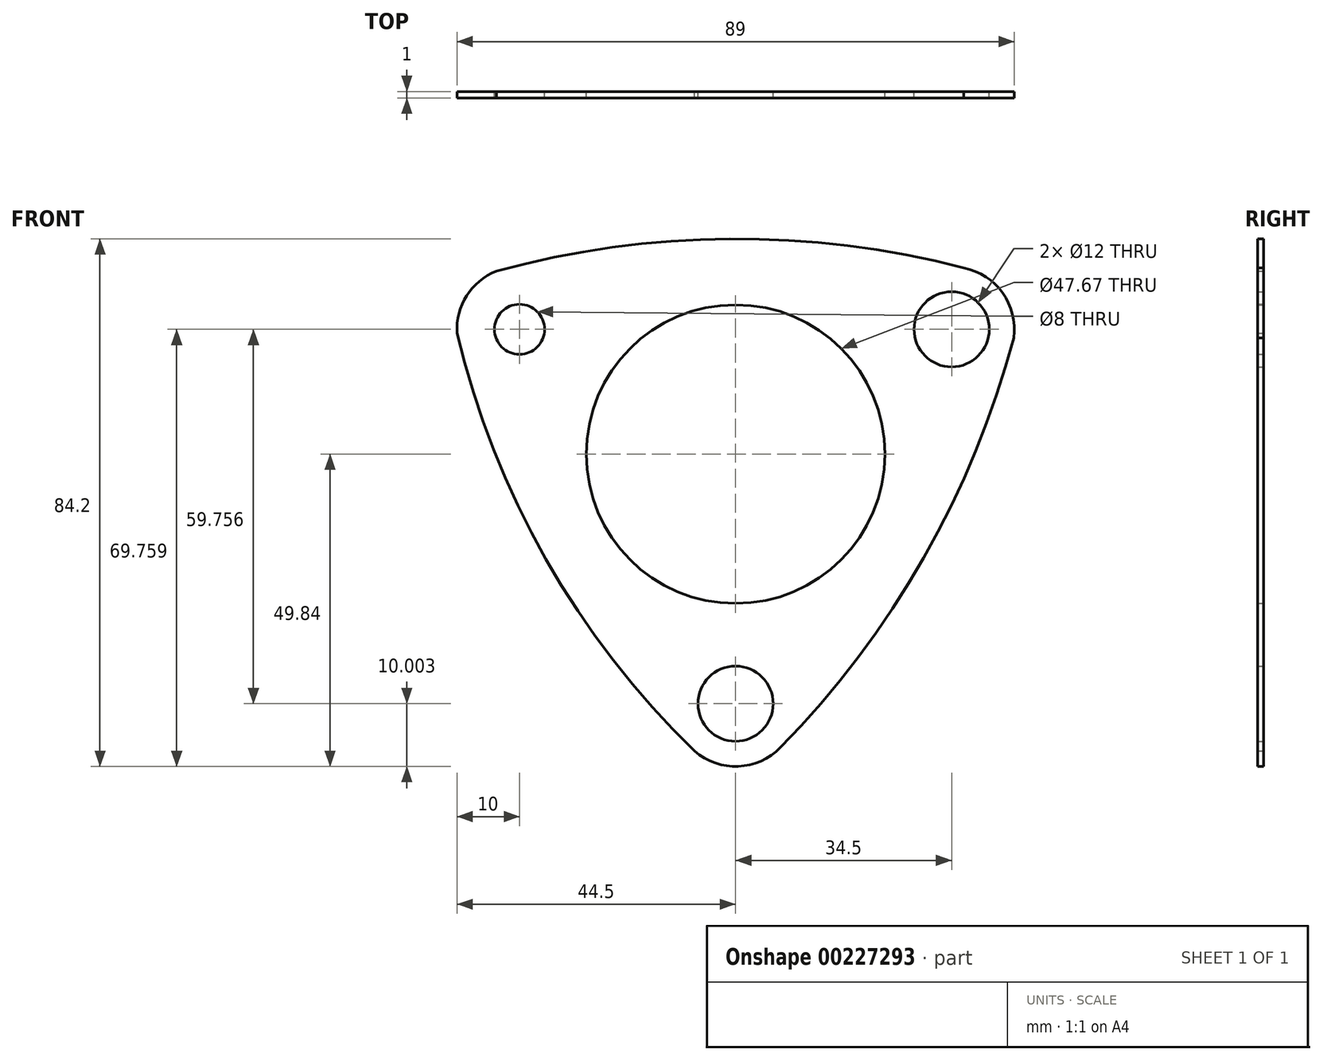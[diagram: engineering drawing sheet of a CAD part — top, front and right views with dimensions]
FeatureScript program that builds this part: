
annotation { "Feature Type Name" : "Feature", "Feature Type Description" : "" }
export const myFeature = defineFeature(function(context is Context, id is Id, definition is map)
    precondition{}
    {
        {
            var Q0;
            Q0=qCreatedBy(makeId("Front.planeOp"),FACE);
            var sketch = newSketch(context, id + "F0", { "sketchPlane" : qUnion([Q0])});
            skCircle(sketch, "E0", {"center": v(0, 0) * mm, "radius": 23.84 * mm});
            skCircle(sketch, "E1", {"center": v(34.5, 19.92) * mm, "radius": 6 * mm});
            skCircle(sketch, "E2", {"center": v(0, -39.84) * mm, "radius": 6 * mm});
            skCircle(sketch, "E3", {"center": v(-34.5, 19.92) * mm, "radius": 4 * mm});
            skArc(sketch, "E4", {"start": v(-38.2, 29.2) * mm, "mid": v(-42.95, 25.27) * mm, "end": v(-44.48, 19.31) * mm});
            skArc(sketch, "E5", {"start": v(44.4, 18.56) * mm, "mid": v(42.64, 25.72) * mm, "end": v(36.44, 29.73) * mm});
            skArc(sketch, "E6", {"start": v(-6.54, -47.4) * mm, "mid": v(0.43, -49.83) * mm, "end": v(7.17, -46.8) * mm});
            skArc(sketch, "E7", {"start": v(36.44, 29.73) * mm, "mid": v(-0.92, 34.36) * mm, "end": v(-38.2, 29.2) * mm});
            skArc(sketch, "E8", {"start": v(7.17, -46.8) * mm, "mid": v(30.04, -16.55) * mm, "end": v(44.4, 18.56) * mm});
            skArc(sketch, "E9", {"start": v(-44.48, 19.31) * mm, "mid": v(-30.28, -16.75) * mm, "end": v(-6.54, -47.4) * mm});
            skSolve(sketch);
        }
        {
            var Q0;
            Q0=makeQuery(id+"F0.imprint","IMPRINT",FACE,{"disambiguationData":[TD([[makeQuery(id+"F0.imprint","IMPRINT",EDGE,{"derivedFrom":sQuery(id+"F0.wireOp",EDGE,"E0")}),-1.0]])]});
            extrude(context, id + "F1", {"entities" : qUnion([Q0]), "depth" : 1 * mm});
        }
    });
